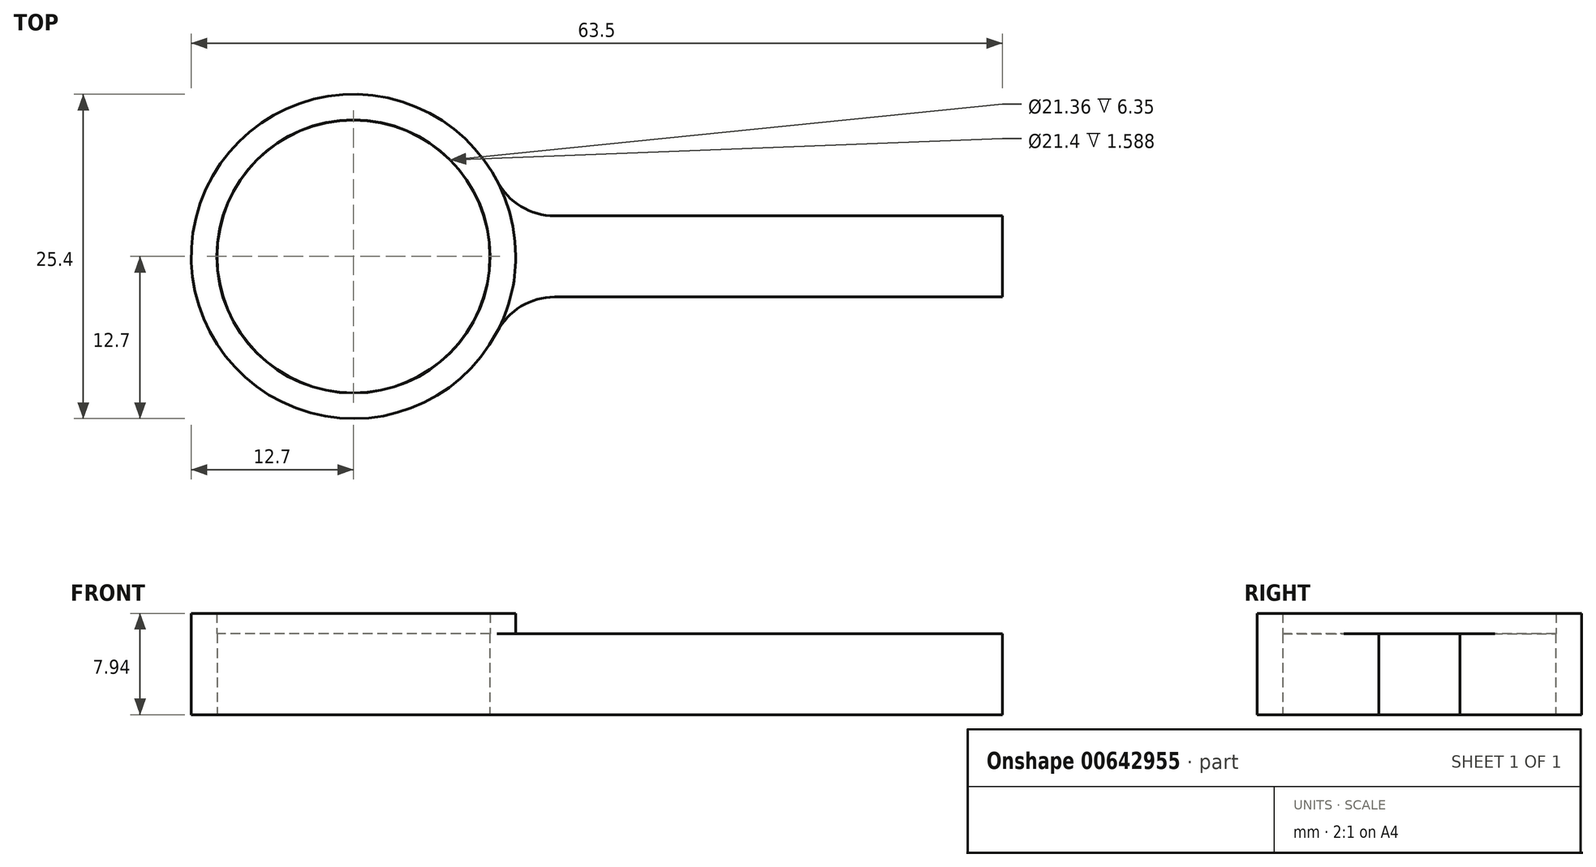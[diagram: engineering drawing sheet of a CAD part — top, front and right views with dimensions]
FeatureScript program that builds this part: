
annotation { "Feature Type Name" : "Feature", "Feature Type Description" : "" }
export const myFeature = defineFeature(function(context is Context, id is Id, definition is map)
    precondition{}
    {
        {
            var Q0;
            Q0=qCreatedBy(makeId("Top.planeOp"),FACE);
            var sketch = newSketch(context, id + "F0", { "sketchPlane" : qUnion([Q0])});
            skArc(sketch, "E0", {"start": v(12.3, 3.18) * mm, "mid": v(-12.7, 0) * mm, "end": v(12.3, -3.18) * mm});
            skPoint(sketch, "E1.orphan", {"position": v(0, 5.18) * mm});
            skLineSegment(sketch, "E2", {"start": v(0, 0) * mm, "end": v(0, -3.18) * mm});
            skLineSegment(sketch, "E3", {"start": v(12.3, -3.18) * mm, "end": v(50.8, -3.18) * mm});
            skLineSegment(sketch, "E4", {"start": v(50.8, -3.18) * mm, "end": v(50.8, 3.18) * mm});
            skLineSegment(sketch, "E5", {"start": v(50.8, 3.18) * mm, "end": v(12.3, 3.18) * mm});
            skCircle(sketch, "E6", {"center": v(0, 0) * mm, "radius": 10.68 * mm});
            skPoint(sketch, "E7.orphan", {"position": v(0, 3.18) * mm});
            skSolve(sketch);
        }
        {
            var Q0;
            Q0=makeQuery(id+"F0.imprint","IMPRINT",FACE,{"disambiguationData":[TD([[makeQuery(id+"F0.imprint","IMPRINT",EDGE,{"derivedFrom":sQuery(id+"F0.wireOp",EDGE,"E0")}),1.0]])]});
            extrude(context, id + "F1", {"entities" : qUnion([Q0]), "depth" : 6.35 * mm, "offsetDistance" : 25.4 * mm});
        }
        {
            var Q0;
            Q0=makeQuery(id+"F1.opExtrude","CAP_FACE",FACE,{"disambiguationData":[OSD([sQuery(id+"F0.wireOp",EDGE,"E0"),sQuery(id+"F0.wireOp",EDGE,"E3"),sQuery(id+"F0.wireOp",EDGE,"E4"),sQuery(id+"F0.wireOp",EDGE,"E5"),sQuery(id+"F0.wireOp",EDGE,"E6")])],"isStart":false});
            var sketch = newSketch(context, id + "F2", { "sketchPlane" : qUnion([Q0])});
            skCircle(sketch, "E8", {"center": v(0, 0) * mm, "radius": 12.7 * mm});
            skCircle(sketch, "E9", {"center": v(0, 0) * mm, "radius": 10.7 * mm});
            skSolve(sketch);
        }
        {
            var Q0;
            Q0=makeQuery(id+"F2.imprint","IMPRINT",FACE,{"disambiguationData":[TD([[makeQuery(id+"F2.imprint","IMPRINT",EDGE,{"derivedFrom":sQuery(id+"F2.wireOp",EDGE,"E9")}),-1.0]])]});
            extrude(context, id + "F3", {"entities" : qUnion([Q0]), "operationType" : NewBodyOperationType.ADD, "depth" : 1.59 * mm, "offsetDistance" : 25.4 * mm});
        }
        {
            var Q0;
            Q0=makeQuery(id+"F1.opExtrude","SWEPT_EDGE",EDGE,{"disambiguationData":[OSD([sQuery(id+"F0.wireOp",EDGE,"E0"),sQuery(id+"F0.wireOp",EDGE,"E3")])]});
            fillet(context, id + "F4", {"entities" : qUnion([Q0]), "radius" : 5.08 * mm, "tangentPropagation" : true, "allowEdgeOverflow" : false});
        }
        {
            var Q0;
            Q0=makeQuery(id+"F1.opExtrude","SWEPT_EDGE",EDGE,{"disambiguationData":[OSD([sQuery(id+"F0.wireOp",EDGE,"E0"),sQuery(id+"F0.wireOp",EDGE,"E5")])]});
            fillet(context, id + "F5", {"entities" : qUnion([Q0]), "radius" : 5.08 * mm, "tangentPropagation" : true, "allowEdgeOverflow" : false});
        }
    });
